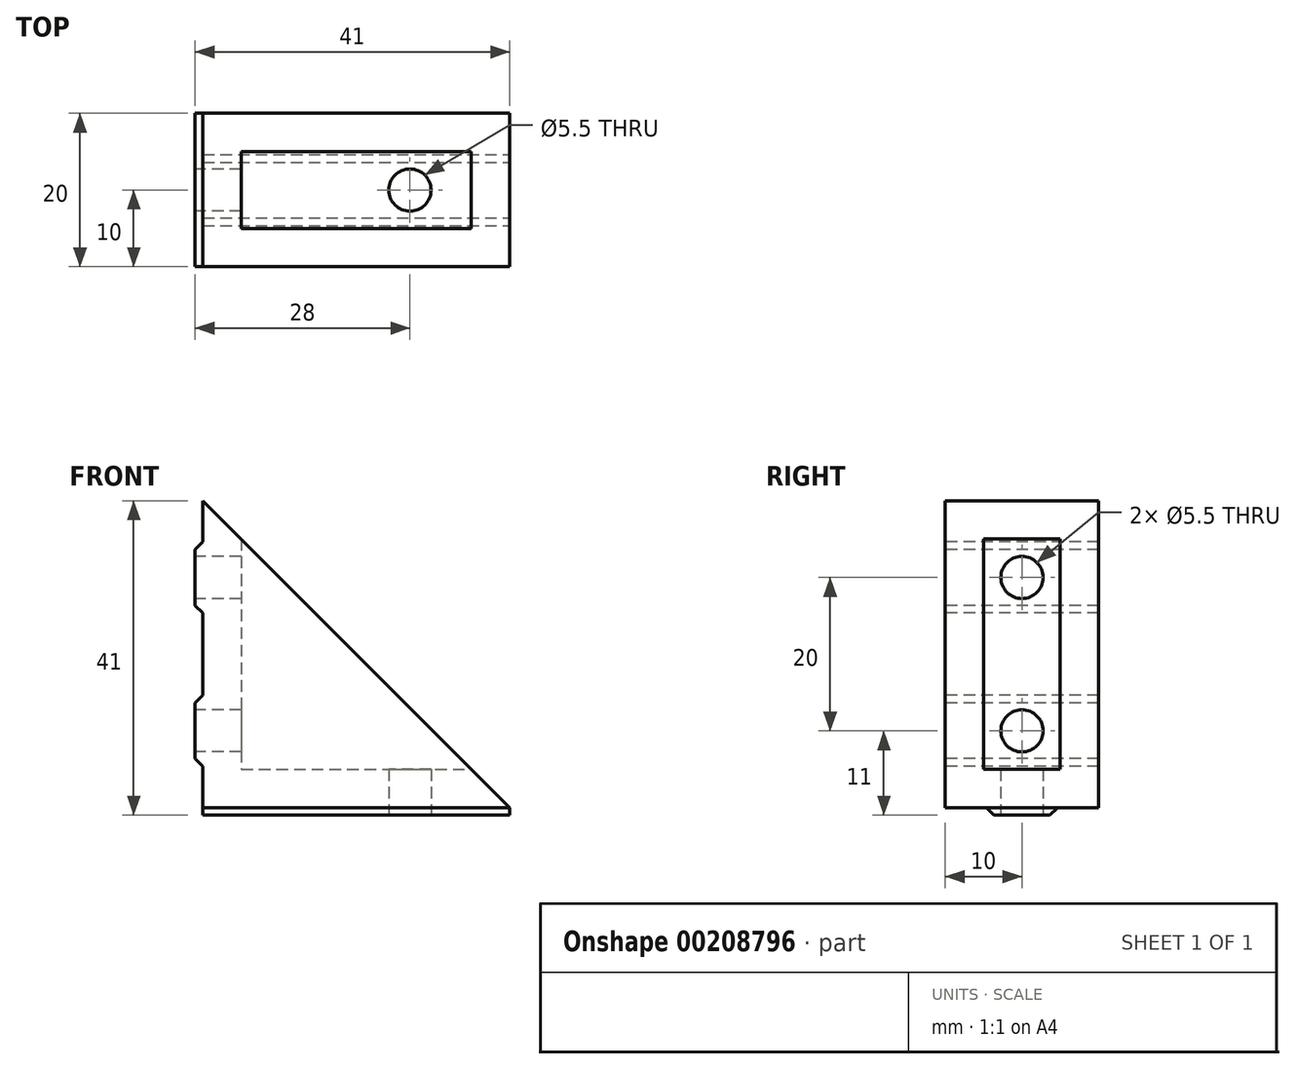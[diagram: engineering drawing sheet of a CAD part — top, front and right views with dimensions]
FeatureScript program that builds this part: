
annotation { "Feature Type Name" : "Feature", "Feature Type Description" : "" }
export const myFeature = defineFeature(function(context is Context, id is Id, definition is map)
    precondition{}
    {
        {
            var Q0;
            Q0=qCreatedBy(makeId("Top.planeOp"),FACE);
            var sketch = newSketch(context, id + "F0", { "sketchPlane" : qUnion([Q0])});
            skLineSegment(sketch, "E0.bottom", {"start": v(0, 0) * mm, "end": v(40, 0) * mm});
            skLineSegment(sketch, "E0.top", {"start": v(0, -20) * mm, "end": v(40, -20) * mm});
            skLineSegment(sketch, "E0.left", {"start": v(0, 0) * mm, "end": v(0, -20) * mm});
            skLineSegment(sketch, "E0.right", {"start": v(40, 0) * mm, "end": v(40, -20) * mm});
            skSolve(sketch);
        }
        {
            var Q0;
            Q0=makeQuery(id+"F0.imprint","IMPRINT",FACE,{"disambiguationData":[TD([[makeQuery(id+"F0.imprint","IMPRINT",EDGE,{"derivedFrom":sQuery(id+"F0.wireOp",EDGE,"E0.bottom")}),-1.0]])]});
            extrude(context, id + "F1", {"entities" : qUnion([Q0]), "depth" : 5 * mm});
        }
        {
            var Q0;
            Q0=makeQuery(id+"F1.opExtrude","CAP_FACE",FACE,{"disambiguationData":[OSD([sQuery(id+"F0.wireOp",EDGE,"E0.bottom"),sQuery(id+"F0.wireOp",EDGE,"E0.top"),sQuery(id+"F0.wireOp",EDGE,"E0.left"),sQuery(id+"F0.wireOp",EDGE,"E0.right")])],"isStart":false});
            var sketch = newSketch(context, id + "F2", { "sketchPlane" : qUnion([Q0])});
            skLineSegment(sketch, "E1", {"start": v(40, -20) * mm, "end": v(40, -15) * mm});
            skLineSegment(sketch, "E2", {"start": v(40, -15) * mm, "end": v(5, -15) * mm});
            skLineSegment(sketch, "E3", {"start": v(5, -15) * mm, "end": v(5, -5) * mm});
            skLineSegment(sketch, "E4", {"start": v(5, -5) * mm, "end": v(40, -5) * mm});
            skLineSegment(sketch, "E5", {"start": v(40, -5) * mm, "end": v(40, 0) * mm});
            skLineSegment(sketch, "E6", {"start": v(40, 0) * mm, "end": v(0, 0) * mm});
            skLineSegment(sketch, "E7", {"start": v(0, 0) * mm, "end": v(0, -20) * mm});
            skLineSegment(sketch, "E8", {"start": v(0, -20) * mm, "end": v(40, -20) * mm});
            skSolve(sketch);
        }
        {
            var Q0;
            Q0=makeQuery(id+"F2.imprint","IMPRINT",FACE,{"disambiguationData":[TD([[makeQuery(id+"F2.imprint","IMPRINT",EDGE,{"derivedFrom":sQuery(id+"F2.wireOp",EDGE,"E1")}),-1.0]])]});
            extrude(context, id + "F3", {"entities" : qUnion([Q0]), "operationType" : NewBodyOperationType.ADD, "depth" : 35 * mm});
        }
        {
            var Q0;
            Q0=makeQuery(id+"F3.boolean.opBoolean","MERGE",FACE,{"derivedFrom":[makeQuery(id+"F1.opExtrude","SWEPT_FACE",FACE,{"disambiguationData":[OSD([sQuery(id+"F0.wireOp",EDGE,"E0.right")])]}),makeQuery(id+"F3.opExtrude","SWEPT_FACE",FACE,{"disambiguationData":[OSD([sQuery(id+"F2.wireOp",EDGE,"E1")])]}),makeQuery(id+"F3.opExtrude","SWEPT_FACE",FACE,{"disambiguationData":[OSD([sQuery(id+"F2.wireOp",EDGE,"E5")])]})]});
            var sketch = newSketch(context, id + "F4", { "sketchPlane" : qUnion([Q0])});
            skLineSegment(sketch, "E9", {"start": v(-20, 0) * mm, "end": v(-14.64, 0) * mm, "construction": true});
            skLineSegment(sketch, "E10", {"start": v(-14.64, 0) * mm, "end": v(-5.36, 0) * mm});
            skLineSegment(sketch, "E11", {"start": v(-5.36, 0) * mm, "end": v(0, 0) * mm, "construction": true});
            skLineSegment(sketch, "E12", {"start": v(-5.36, 0) * mm, "end": v(-6.36, -1) * mm});
            skLineSegment(sketch, "E13", {"start": v(-6.36, -1) * mm, "end": v(-7.16, -1.8) * mm, "construction": true});
            skLineSegment(sketch, "E14", {"start": v(-7.16, -1.8) * mm, "end": v(-10, -4.64) * mm, "construction": true});
            skLineSegment(sketch, "E15", {"start": v(-10, -4.64) * mm, "end": v(-12.84, -1.8) * mm, "construction": true});
            skLineSegment(sketch, "E16", {"start": v(-12.84, -1.8) * mm, "end": v(-13.64, -1) * mm, "construction": true});
            skLineSegment(sketch, "E17", {"start": v(-13.64, -1) * mm, "end": v(-14.64, 0) * mm});
            skLineSegment(sketch, "E18", {"start": v(-13.64, -1) * mm, "end": v(-6.36, -1) * mm});
            skLineSegment(sketch, "E19", {"start": v(-7.16, -1.8) * mm, "end": v(-12.84, -1.8) * mm, "construction": true});
            skLineSegment(sketch, "E20", {"start": v(-10, -1) * mm, "end": v(-10, 0) * mm, "construction": true});
            skSolve(sketch);
        }
        {
            var Q0;
            Q0=makeQuery(id+"F4.imprint","IMPRINT",FACE,{"disambiguationData":[TD([[makeQuery(id+"F4.imprint","IMPRINT",EDGE,{"derivedFrom":sQuery(id+"F4.wireOp",EDGE,"E10")}),1.0]])]});
            var Q1;
            Q1=sQuery(id+"F4.wireOp",EDGE,"E16");
            var Q2;
            Q2=makeQuery(id+"F3.boolean.opBoolean","MERGE",FACE,{"derivedFrom":[makeQuery(id+"F1.opExtrude","SWEPT_FACE",FACE,{"disambiguationData":[OSD([sQuery(id+"F0.wireOp",EDGE,"E0.left")])]}),makeQuery(id+"F3.opExtrude","SWEPT_FACE",FACE,{"disambiguationData":[OSD([sQuery(id+"F2.wireOp",EDGE,"E7")])]})]});
            extrude(context, id + "F5", {"entities" : qUnion([Q0]), "operationType" : NewBodyOperationType.ADD, "surfaceEntities" : qUnion([Q1]), "endBound" : BoundingType.UP_TO_SURFACE, "oppositeDirection" : true, "endBoundEntityFace" : qUnion([Q2]), "depth" : 25 * mm});
        }
        {
            var Q0;
            Q0=makeQuery(id+"F3.boolean.opBoolean","MERGE",FACE,{"derivedFrom":[makeQuery(id+"F1.opExtrude","SWEPT_FACE",FACE,{"disambiguationData":[OSD([sQuery(id+"F0.wireOp",EDGE,"E0.top")])]}),makeQuery(id+"F3.opExtrude","SWEPT_FACE",FACE,{"disambiguationData":[OSD([sQuery(id+"F2.wireOp",EDGE,"E8")])]})]});
            var sketch = newSketch(context, id + "F6", { "sketchPlane" : qUnion([Q0])});
            skLineSegment(sketch, "E21", {"start": v(0, 40) * mm, "end": v(40, 0) * mm});
            skLineSegment(sketch, "E22", {"start": v(40, 0) * mm, "end": v(40, 40) * mm});
            skLineSegment(sketch, "E23", {"start": v(40, 40) * mm, "end": v(0, 40) * mm});
            skSolve(sketch);
        }
        {
            var Q0;
            Q0=makeQuery(id+"F6.imprint","IMPRINT",FACE,{"disambiguationData":[TD([[makeQuery(id+"F6.imprint","IMPRINT",EDGE,{"derivedFrom":sQuery(id+"F6.wireOp",EDGE,"E21")}),1.0]])]});
            extrude(context, id + "F7", {"entities" : qUnion([Q0]), "operationType" : NewBodyOperationType.REMOVE, "endBound" : BoundingType.THROUGH_ALL, "oppositeDirection" : true, "depth" : 25 * mm});
        }
        {
            var Q0;
            Q0=makeQuery(id+"F3.boolean.opBoolean","MERGE",FACE,{"derivedFrom":[makeQuery(id+"F1.opExtrude","SWEPT_FACE",FACE,{"disambiguationData":[OSD([sQuery(id+"F0.wireOp",EDGE,"E0.top")])]}),makeQuery(id+"F3.opExtrude","SWEPT_FACE",FACE,{"disambiguationData":[OSD([sQuery(id+"F2.wireOp",EDGE,"E8")])]})]});
            var sketch = newSketch(context, id + "F8", { "sketchPlane" : qUnion([Q0])});
            skLineSegment(sketch, "E24", {"start": v(0, 40) * mm, "end": v(0, 34.64) * mm, "construction": true});
            skLineSegment(sketch, "E25", {"start": v(0, 34.64) * mm, "end": v(0, 25.36) * mm});
            skLineSegment(sketch, "E26", {"start": v(0, 25.36) * mm, "end": v(0, 14.64) * mm, "construction": true});
            skLineSegment(sketch, "E27", {"start": v(0, 14.64) * mm, "end": v(0, 5.36) * mm});
            skLineSegment(sketch, "E28", {"start": v(0, 5.36) * mm, "end": v(0, 0) * mm, "construction": true});
            skLineSegment(sketch, "E29", {"start": v(0, 14.64) * mm, "end": v(-1, 13.64) * mm});
            skLineSegment(sketch, "E30", {"start": v(-1, 13.64) * mm, "end": v(-1.8, 12.84) * mm, "construction": true});
            skLineSegment(sketch, "E31", {"start": v(-1.8, 12.84) * mm, "end": v(-4.64, 10) * mm, "construction": true});
            skLineSegment(sketch, "E32", {"start": v(-4.64, 10) * mm, "end": v(-1.8, 7.16) * mm, "construction": true});
            skLineSegment(sketch, "E33", {"start": v(-1.8, 7.16) * mm, "end": v(-1, 6.36) * mm, "construction": true});
            skLineSegment(sketch, "E34", {"start": v(-1, 6.36) * mm, "end": v(0, 5.36) * mm});
            skLineSegment(sketch, "E35", {"start": v(0, 25.36) * mm, "end": v(-1, 26.36) * mm});
            skLineSegment(sketch, "E36", {"start": v(-1, 26.36) * mm, "end": v(-1.8, 27.16) * mm, "construction": true});
            skLineSegment(sketch, "E37", {"start": v(-1.8, 27.16) * mm, "end": v(-4.64, 30) * mm, "construction": true});
            skLineSegment(sketch, "E38", {"start": v(-4.64, 30) * mm, "end": v(-1.8, 32.84) * mm, "construction": true});
            skLineSegment(sketch, "E39", {"start": v(-1.8, 32.84) * mm, "end": v(-1, 33.64) * mm, "construction": true});
            skLineSegment(sketch, "E40", {"start": v(-1, 33.64) * mm, "end": v(0, 34.64) * mm});
            skLineSegment(sketch, "E41", {"start": v(-1, 33.64) * mm, "end": v(-1, 26.36) * mm});
            skLineSegment(sketch, "E42", {"start": v(-1.8, 27.16) * mm, "end": v(-1.8, 32.84) * mm, "construction": true});
            skLineSegment(sketch, "E43", {"start": v(-1.8, 12.84) * mm, "end": v(-1.8, 7.16) * mm, "construction": true});
            skLineSegment(sketch, "E44", {"start": v(-1, 6.36) * mm, "end": v(-1, 13.64) * mm});
            skLineSegment(sketch, "E45", {"start": v(-1, 10) * mm, "end": v(0, 10) * mm, "construction": true});
            skLineSegment(sketch, "E46", {"start": v(-1, 30) * mm, "end": v(0, 30) * mm, "construction": true});
            skSolve(sketch);
        }
        {
            var Q0;
            Q0=makeQuery(id+"F8.imprint","IMPRINT",FACE,{"disambiguationData":[TD([[makeQuery(id+"F8.imprint","IMPRINT",EDGE,{"derivedFrom":sQuery(id+"F8.wireOp",EDGE,"E25")}),-1.0]])]});
            var Q1;
            Q1=makeQuery(id+"F8.imprint","IMPRINT",FACE,{"disambiguationData":[TD([[makeQuery(id+"F8.imprint","IMPRINT",EDGE,{"derivedFrom":sQuery(id+"F8.wireOp",EDGE,"E27")}),-1.0]])]});
            var Q2;
            Q2=sQuery(id+"F8.wireOp",EDGE,"E28");
            var Q3;
            Q3=sQuery(id+"F8.wireOp",EDGE,"E43");
            var Q4;
            Q4=sQuery(id+"F8.wireOp",EDGE,"E45");
            var Q5;
            Q5=sQuery(id+"F8.wireOp",EDGE,"E33");
            var Q6;
            Q6=sQuery(id+"F8.wireOp",EDGE,"E30");
            var Q7;
            Q7=sQuery(id+"F8.wireOp",EDGE,"E31");
            var Q8;
            Q8=sQuery(id+"F8.wireOp",EDGE,"E32");
            var Q9;
            Q9=makeQuery(id+"F3.boolean.opBoolean","MERGE",FACE,{"derivedFrom":[makeQuery(id+"F1.opExtrude","SWEPT_FACE",FACE,{"disambiguationData":[OSD([sQuery(id+"F0.wireOp",EDGE,"E0.bottom")])]}),makeQuery(id+"F3.opExtrude","SWEPT_FACE",FACE,{"disambiguationData":[OSD([sQuery(id+"F2.wireOp",EDGE,"E6")])]})]});
            extrude(context, id + "F9", {"entities" : qUnion([Q0, Q1]), "operationType" : NewBodyOperationType.ADD, "surfaceEntities" : qUnion([Q2, Q3, Q4, Q5, Q6, Q7, Q8]), "endBound" : BoundingType.UP_TO_SURFACE, "oppositeDirection" : true, "endBoundEntityFace" : qUnion([Q9]), "depth" : 25 * mm});
        }
        {
            var Q0;
            Q0=makeQuery(id+"F3.opExtrude","SWEPT_FACE",FACE,{"disambiguationData":[OSD([sQuery(id+"F2.wireOp",EDGE,"E3")])]});
            var sketch = newSketch(context, id + "F10", { "sketchPlane" : qUnion([Q0])});
            skLineSegment(sketch, "E47", {"start": v(-10, 35) * mm, "end": v(-10, 30) * mm, "construction": true});
            skLineSegment(sketch, "E48", {"start": v(-10, 30) * mm, "end": v(-10, 10) * mm, "construction": true});
            skLineSegment(sketch, "E49", {"start": v(-10, 10) * mm, "end": v(-10, 5) * mm, "construction": true});
            skSolve(sketch);
        }
        {
            var Q0;
            Q0=makeQuery(id+"F1.opExtrude","CAP_FACE",FACE,{"disambiguationData":[OSD([sQuery(id+"F0.wireOp",EDGE,"E0.bottom"),sQuery(id+"F0.wireOp",EDGE,"E0.top"),sQuery(id+"F0.wireOp",EDGE,"E0.left"),sQuery(id+"F0.wireOp",EDGE,"E0.right")])],"isStart":false});
            var sketch = newSketch(context, id + "F11", { "sketchPlane" : qUnion([Q0])});
            skLineSegment(sketch, "E50", {"start": v(5, -10) * mm, "end": v(17, -10) * mm});
            skLineSegment(sketch, "E51", {"start": v(17, -10) * mm, "end": v(27, -10) * mm});
            skLineSegment(sketch, "E52", {"start": v(27, -10) * mm, "end": v(35, -10) * mm});
            skSolve(sketch);
        }
        {
            var Q0;
            Q0=sQuery(id+"F10.wireOp",VERTEX,"E48.start");
            var Q1;
            Q1=sQuery(id+"F10.wireOp",VERTEX,"E49.start");
            var Q2;
            Q2=sQuery(id+"F11.wireOp",VERTEX,"E52.start");
            var Q3;
            Q3=makeQuery(id+"F1.opExtrude","SWEPT_BODY",BODY,{"disambiguationData":[OSD([sQuery(id+"F0.wireOp",EDGE,"E0.bottom"),sQuery(id+"F0.wireOp",EDGE,"E0.top"),sQuery(id+"F0.wireOp",EDGE,"E0.left"),sQuery(id+"F0.wireOp",EDGE,"E0.right")])]});
            hole(context, id + "F12", {"style" : HoleStyle.SIMPLE, "endStyle" : HoleEndStyle.THROUGH, "standardTappedOrClearance" : lookupTablePath({ "standard" : "ISO", "fit" : "Normal", "size" : "M5", "type" : "Clearance" }), "standardBlindInLast" : lookupTablePath({ "fit" : "Standard", "standard" : "ISO", "size" : "M5", "type" : "Clearance" }), "holeDiameter" : 5.5 * mm, "locations" : qUnion([Q0, Q1, Q2]), "scope" : qUnion([Q3]), "isTappedThrough" : true});
        }
    });
